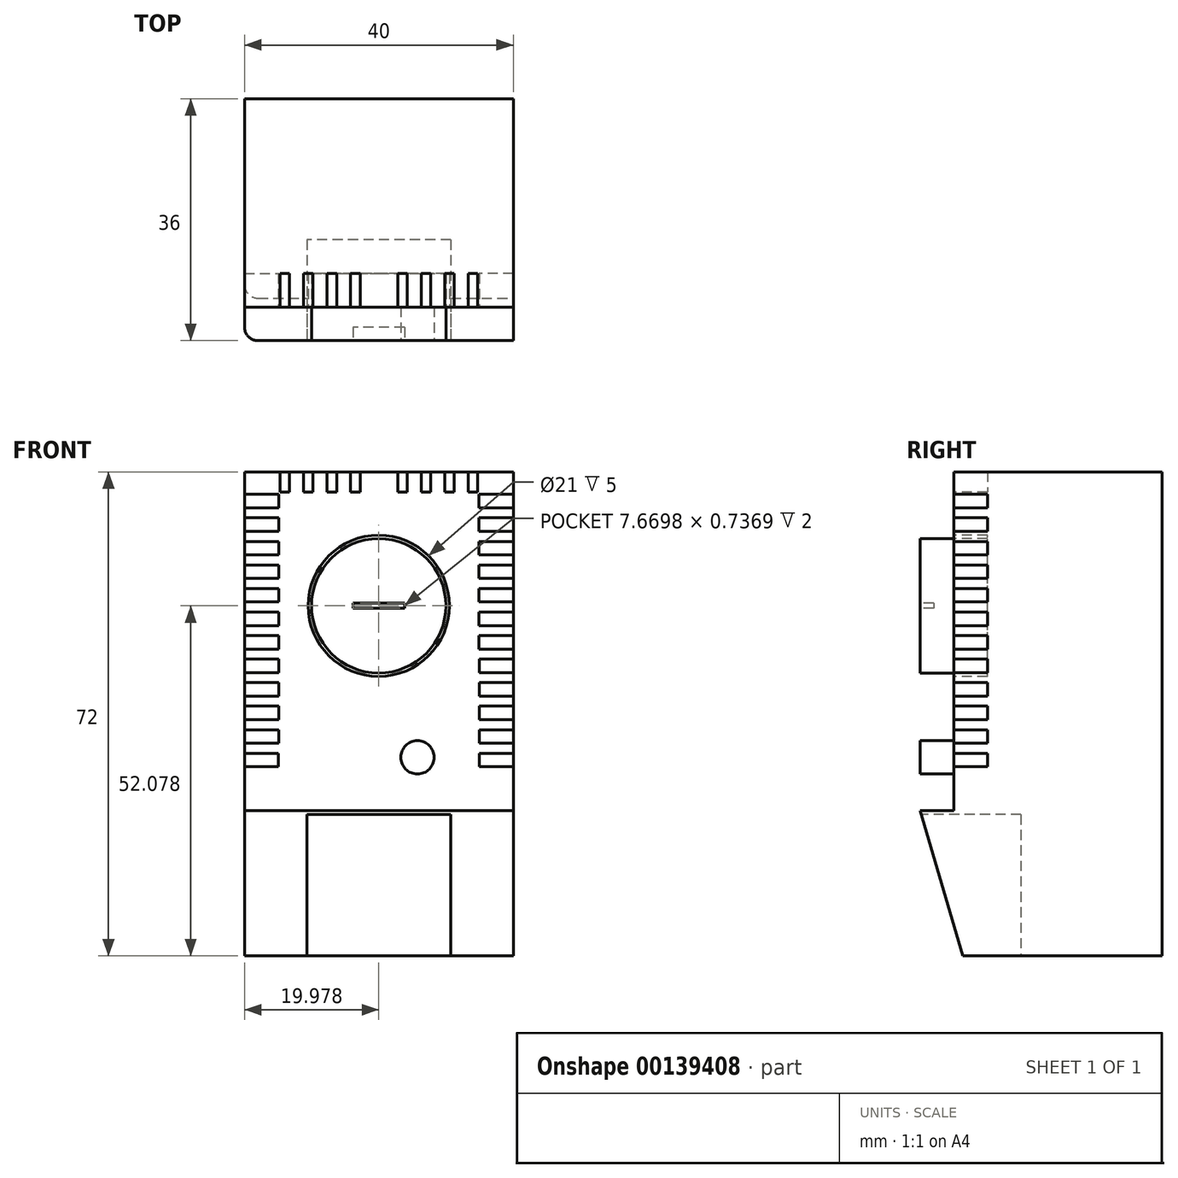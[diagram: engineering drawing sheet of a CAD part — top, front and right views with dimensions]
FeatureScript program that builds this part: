
annotation { "Feature Type Name" : "Feature", "Feature Type Description" : "" }
export const myFeature = defineFeature(function(context is Context, id is Id, definition is map)
    precondition{}
    {
        {
            var Q0;
            Q0=qCreatedBy(makeId("Front.planeOp"),FACE);
            var sketch = newSketch(context, id + "F0", { "sketchPlane" : qUnion([Q0])});
            skLineSegment(sketch, "E0.bottom", {"start": v(-33, 26.48) * mm, "end": v(7, 26.48) * mm});
            skLineSegment(sketch, "E0.top", {"start": v(-33, -45.52) * mm, "end": v(7, -45.52) * mm});
            skLineSegment(sketch, "E0.left", {"start": v(-33, 26.48) * mm, "end": v(-33, -45.52) * mm});
            skLineSegment(sketch, "E0.right", {"start": v(7, 26.48) * mm, "end": v(7, -45.52) * mm});
            skSolve(sketch);
        }
        {
            var Q0;
            Q0=makeQuery(id+"F0.imprint","IMPRINT",FACE,{"disambiguationData":[TD([[makeQuery(id+"F0.imprint","IMPRINT",EDGE,{"derivedFrom":sQuery(id+"F0.wireOp",EDGE,"E0.bottom")}),-1.0]])]});
            extrude(context, id + "F1", {"entities" : qUnion([Q0]), "depth" : 36 * mm});
        }
        {
            var Q0;
            Q0=makeQuery(id+"F1.opExtrude","CAP_FACE",FACE,{"disambiguationData":[OSD([sQuery(id+"F0.wireOp",EDGE,"E0.bottom"),sQuery(id+"F0.wireOp",EDGE,"E0.top"),sQuery(id+"F0.wireOp",EDGE,"E0.left"),sQuery(id+"F0.wireOp",EDGE,"E0.right")])],"isStart":false});
            var sketch = newSketch(context, id + "F2", { "sketchPlane" : qUnion([Q0])});
            skCircle(sketch, "E1", {"center": v(-13.03, 6.56) * mm, "radius": 10 * mm});
            skCircle(sketch, "E2.0", {"center": v(-13.03, 6.56) * mm, "radius": 10.5 * mm});
            skLineSegment(sketch, "E3.bottom", {"start": v(-9.1, 7.18) * mm, "end": v(-16.96, 7.18) * mm});
            skLineSegment(sketch, "E3.top", {"start": v(-9.1, 5.94) * mm, "end": v(-16.96, 5.94) * mm});
            skLineSegment(sketch, "E3.left", {"start": v(-9.1, 7.18) * mm, "end": v(-9.1, 5.94) * mm});
            skLineSegment(sketch, "E3.right", {"start": v(-16.96, 7.18) * mm, "end": v(-16.96, 5.94) * mm});
            skLineSegment(sketch, "E4.bottom", {"start": v(-33, 23.12) * mm, "end": v(-27.9, 23.12) * mm});
            skLineSegment(sketch, "E4.top", {"start": v(-33, 21.12) * mm, "end": v(-27.9, 21.12) * mm});
            skLineSegment(sketch, "E4.left", {"start": v(-33, 23.12) * mm, "end": v(-33, 21.12) * mm});
            skLineSegment(sketch, "E4.right", {"start": v(-27.9, 23.12) * mm, "end": v(-27.9, 21.12) * mm});
            skLineSegment(sketch, "E5.top", {"start": v(-12.3, 23.45) * mm, "end": v(-13.72, 23.45) * mm});
            skLineSegment(sketch, "E5.left", {"start": v(-12.3, 26.48) * mm, "end": v(-12.3, 23.45) * mm});
            skLineSegment(sketch, "E5.right", {"start": v(-13.72, 26.48) * mm, "end": v(-13.72, 23.45) * mm});
            skPoint(sketch, "E5.middle", {"position": v(-13, 26.48) * mm});
            skLineSegment(sketch, "E6", {"start": v(-13.72, 26.48) * mm, "end": v(-12.3, 26.48) * mm});
            skLineSegment(sketch, "E7.1.0.0", {"start": v(-33, 19.62) * mm, "end": v(-33, 17.62) * mm});
            skLineSegment(sketch, "E7.1.0.1", {"start": v(-33, 19.62) * mm, "end": v(-27.9, 19.62) * mm});
            skLineSegment(sketch, "E7.1.0.2", {"start": v(-27.9, 19.62) * mm, "end": v(-27.9, 17.62) * mm});
            skLineSegment(sketch, "E7.1.0.3", {"start": v(-33, 17.62) * mm, "end": v(-27.9, 17.62) * mm});
            skLineSegment(sketch, "E7.2.0.0", {"start": v(-33.01, 16.12) * mm, "end": v(-33.01, 14.12) * mm});
            skLineSegment(sketch, "E7.2.0.1", {"start": v(-33.01, 16.12) * mm, "end": v(-27.9, 16.12) * mm});
            skLineSegment(sketch, "E7.2.0.2", {"start": v(-27.9, 16.12) * mm, "end": v(-27.9, 14.12) * mm});
            skLineSegment(sketch, "E7.2.0.3", {"start": v(-33.01, 14.12) * mm, "end": v(-27.9, 14.12) * mm});
            skLineSegment(sketch, "E7.3.0.0", {"start": v(-33.02, 12.62) * mm, "end": v(-33.02, 10.62) * mm});
            skLineSegment(sketch, "E7.3.0.1", {"start": v(-33.02, 12.62) * mm, "end": v(-27.9, 12.62) * mm});
            skLineSegment(sketch, "E7.3.0.2", {"start": v(-27.9, 12.62) * mm, "end": v(-27.9, 10.62) * mm});
            skLineSegment(sketch, "E7.3.0.3", {"start": v(-33.02, 10.62) * mm, "end": v(-27.9, 10.62) * mm});
            skLineSegment(sketch, "E7.4.0.0", {"start": v(-33.02, 9.12) * mm, "end": v(-33.02, 7.12) * mm});
            skLineSegment(sketch, "E7.4.0.1", {"start": v(-33.02, 9.12) * mm, "end": v(-27.91, 9.12) * mm});
            skLineSegment(sketch, "E7.4.0.2", {"start": v(-27.91, 9.12) * mm, "end": v(-27.91, 7.12) * mm});
            skLineSegment(sketch, "E7.4.0.3", {"start": v(-33.02, 7.12) * mm, "end": v(-27.91, 7.12) * mm});
            skLineSegment(sketch, "E7.5.0.0", {"start": v(-33.02, 5.62) * mm, "end": v(-33.02, 3.62) * mm});
            skLineSegment(sketch, "E7.5.0.1", {"start": v(-33.02, 5.62) * mm, "end": v(-27.91, 5.62) * mm});
            skLineSegment(sketch, "E7.5.0.2", {"start": v(-27.91, 5.62) * mm, "end": v(-27.91, 3.62) * mm});
            skLineSegment(sketch, "E7.5.0.3", {"start": v(-33.02, 3.62) * mm, "end": v(-27.91, 3.62) * mm});
            skLineSegment(sketch, "E7.6.0.0", {"start": v(-33.03, 2.12) * mm, "end": v(-33.03, 0.12) * mm});
            skLineSegment(sketch, "E7.6.0.1", {"start": v(-33.03, 2.12) * mm, "end": v(-27.92, 2.12) * mm});
            skLineSegment(sketch, "E7.6.0.2", {"start": v(-27.92, 2.12) * mm, "end": v(-27.92, 0.12) * mm});
            skLineSegment(sketch, "E7.6.0.3", {"start": v(-33.03, 0.12) * mm, "end": v(-27.92, 0.12) * mm});
            skLineSegment(sketch, "E7.7.0.0", {"start": v(-33.03, -1.38) * mm, "end": v(-33.03, -3.38) * mm});
            skLineSegment(sketch, "E7.7.0.1", {"start": v(-33.03, -1.38) * mm, "end": v(-27.92, -1.38) * mm});
            skLineSegment(sketch, "E7.7.0.2", {"start": v(-27.92, -1.38) * mm, "end": v(-27.92, -3.38) * mm});
            skLineSegment(sketch, "E7.7.0.3", {"start": v(-33.03, -3.38) * mm, "end": v(-27.92, -3.38) * mm});
            skLineSegment(sketch, "E7.8.0.0", {"start": v(-33.04, -4.88) * mm, "end": v(-33.04, -6.88) * mm});
            skLineSegment(sketch, "E7.8.0.1", {"start": v(-33.04, -4.88) * mm, "end": v(-27.93, -4.88) * mm});
            skLineSegment(sketch, "E7.8.0.2", {"start": v(-27.93, -4.88) * mm, "end": v(-27.93, -6.88) * mm});
            skLineSegment(sketch, "E7.8.0.3", {"start": v(-33.04, -6.88) * mm, "end": v(-27.93, -6.88) * mm});
            skLineSegment(sketch, "E7.9.0.0", {"start": v(-33.04, -8.38) * mm, "end": v(-33.04, -10.38) * mm});
            skLineSegment(sketch, "E7.9.0.1", {"start": v(-33.04, -8.38) * mm, "end": v(-27.93, -8.38) * mm});
            skLineSegment(sketch, "E7.9.0.2", {"start": v(-27.93, -8.38) * mm, "end": v(-27.93, -10.38) * mm});
            skLineSegment(sketch, "E7.9.0.3", {"start": v(-33.04, -10.38) * mm, "end": v(-27.93, -10.38) * mm});
            skLineSegment(sketch, "E7.10.0.0", {"start": v(-33.04, -11.88) * mm, "end": v(-33.04, -13.88) * mm});
            skLineSegment(sketch, "E7.10.0.1", {"start": v(-33.04, -11.88) * mm, "end": v(-27.93, -11.88) * mm});
            skLineSegment(sketch, "E7.10.0.2", {"start": v(-27.93, -11.88) * mm, "end": v(-27.93, -13.88) * mm});
            skLineSegment(sketch, "E7.10.0.3", {"start": v(-33.04, -13.88) * mm, "end": v(-27.93, -13.88) * mm});
            skLineSegment(sketch, "E7.11.0.0", {"start": v(-33.05, -15.38) * mm, "end": v(-33.05, -17.38) * mm});
            skLineSegment(sketch, "E7.11.0.1", {"start": v(-33.05, -15.38) * mm, "end": v(-27.94, -15.38) * mm});
            skLineSegment(sketch, "E7.11.0.2", {"start": v(-27.94, -15.38) * mm, "end": v(-27.94, -17.38) * mm});
            skLineSegment(sketch, "E7.11.0.3", {"start": v(-33.05, -17.38) * mm, "end": v(-27.94, -17.38) * mm});
            skLineSegment(sketch, "E7.direction1", {"start": v(-33, 21.12) * mm, "end": v(-33, 17.62) * mm, "construction": true});
            skLineSegment(sketch, "E8.1.0.0", {"start": v(-8.8, 23.45) * mm, "end": v(-10.22, 23.45) * mm});
            skLineSegment(sketch, "E8.1.0.1", {"start": v(-8.8, 26.48) * mm, "end": v(-8.8, 23.45) * mm});
            skPoint(sketch, "E8.1.0.2", {"position": v(-9.5, 26.48) * mm});
            skLineSegment(sketch, "E8.1.0.3", {"start": v(-10.22, 26.48) * mm, "end": v(-10.22, 23.45) * mm});
            skLineSegment(sketch, "E8.1.0.4", {"start": v(-10.22, 26.48) * mm, "end": v(-8.8, 26.48) * mm});
            skLineSegment(sketch, "E8.2.0.0", {"start": v(-5.3, 23.45) * mm, "end": v(-6.72, 23.45) * mm});
            skLineSegment(sketch, "E8.2.0.1", {"start": v(-5.3, 26.48) * mm, "end": v(-5.3, 23.45) * mm});
            skPoint(sketch, "E8.2.0.2", {"position": v(-6, 26.48) * mm});
            skLineSegment(sketch, "E8.2.0.3", {"start": v(-6.72, 26.48) * mm, "end": v(-6.72, 23.45) * mm});
            skLineSegment(sketch, "E8.2.0.4", {"start": v(-6.72, 26.48) * mm, "end": v(-5.3, 26.48) * mm});
            skLineSegment(sketch, "E8.3.0.0", {"start": v(-1.8, 23.45) * mm, "end": v(-3.22, 23.45) * mm});
            skLineSegment(sketch, "E8.3.0.1", {"start": v(-1.8, 26.48) * mm, "end": v(-1.8, 23.45) * mm});
            skPoint(sketch, "E8.3.0.2", {"position": v(-2.5, 26.48) * mm});
            skLineSegment(sketch, "E8.3.0.3", {"start": v(-3.22, 26.48) * mm, "end": v(-3.22, 23.45) * mm});
            skLineSegment(sketch, "E8.3.0.4", {"start": v(-3.22, 26.48) * mm, "end": v(-1.8, 26.48) * mm});
            skLineSegment(sketch, "E8.4.0.0", {"start": v(1.7, 23.45) * mm, "end": v(0.28, 23.45) * mm});
            skLineSegment(sketch, "E8.4.0.1", {"start": v(1.7, 26.48) * mm, "end": v(1.7, 23.45) * mm});
            skPoint(sketch, "E8.4.0.2", {"position": v(1, 26.48) * mm});
            skLineSegment(sketch, "E8.4.0.3", {"start": v(0.28, 26.48) * mm, "end": v(0.28, 23.45) * mm});
            skLineSegment(sketch, "E8.4.0.4", {"start": v(0.28, 26.48) * mm, "end": v(1.7, 26.48) * mm});
            skLineSegment(sketch, "E8.direction1", {"start": v(-13.72, 23.45) * mm, "end": v(-10.22, 23.45) * mm, "construction": true});
            skLineSegment(sketch, "E9", {"start": v(-13, 26.48) * mm, "end": v(-13, 37.21) * mm});
            skLineSegment(sketch, "E10.MirrorCS", {"start": v(-15.8, 26.48) * mm, "end": v(-17.22, 26.48) * mm});
            skLineSegment(sketch, "E11.MirrorCS", {"start": v(-26.3, 26.48) * mm, "end": v(-27.72, 26.48) * mm});
            skLineSegment(sketch, "E12.MirrorCS", {"start": v(-22.8, 26.48) * mm, "end": v(-24.22, 26.48) * mm});
            skLineSegment(sketch, "E13.MirrorCS", {"start": v(-20.72, 23.45) * mm, "end": v(-19.3, 23.45) * mm});
            skLineSegment(sketch, "E14.MirrorCS", {"start": v(-19.3, 26.48) * mm, "end": v(-20.72, 26.48) * mm});
            skLineSegment(sketch, "E15.MirrorCS", {"start": v(-24.22, 23.45) * mm, "end": v(-22.8, 23.45) * mm});
            skLineSegment(sketch, "E16.MirrorCS", {"start": v(-27.72, 23.45) * mm, "end": v(-26.3, 23.45) * mm});
            skLineSegment(sketch, "E17.MirrorCS", {"start": v(-17.22, 23.45) * mm, "end": v(-15.8, 23.45) * mm});
            skLineSegment(sketch, "E18.MirrorCS", {"start": v(-15.8, 26.48) * mm, "end": v(-15.8, 23.45) * mm});
            skLineSegment(sketch, "E19.MirrorCS", {"start": v(-24.22, 26.48) * mm, "end": v(-24.22, 23.45) * mm});
            skLineSegment(sketch, "E20.MirrorCS", {"start": v(-17.22, 26.48) * mm, "end": v(-17.22, 23.45) * mm});
            skPoint(sketch, "E21.MirrorP", {"position": v(-27, 26.48) * mm});
            skLineSegment(sketch, "E22.MirrorCS", {"start": v(-22.8, 26.48) * mm, "end": v(-22.8, 23.45) * mm});
            skLineSegment(sketch, "E23.MirrorCS", {"start": v(-26.3, 26.48) * mm, "end": v(-26.3, 23.45) * mm});
            skPoint(sketch, "E24.MirrorP", {"position": v(-20, 26.48) * mm});
            skLineSegment(sketch, "E25.MirrorCS", {"start": v(-27.72, 26.48) * mm, "end": v(-27.72, 23.45) * mm});
            skLineSegment(sketch, "E26.MirrorCS", {"start": v(-19.3, 26.48) * mm, "end": v(-19.3, 23.45) * mm});
            skLineSegment(sketch, "E27.MirrorCS", {"start": v(-20.72, 26.48) * mm, "end": v(-20.72, 23.45) * mm});
            skPoint(sketch, "E28.MirrorP", {"position": v(-23.5, 26.48) * mm});
            skPoint(sketch, "E29.MirrorP", {"position": v(-16.5, 26.48) * mm});
            skLineSegment(sketch, "E30.MirrorCS", {"start": v(7, 19.62) * mm, "end": v(7, 17.62) * mm});
            skLineSegment(sketch, "E31.MirrorCS", {"start": v(7.02, 2.12) * mm, "end": v(7.02, 0.12) * mm});
            skLineSegment(sketch, "E32.MirrorCS", {"start": v(7, 23.12) * mm, "end": v(7, 21.12) * mm});
            skLineSegment(sketch, "E33.MirrorCS", {"start": v(1.88, 23.12) * mm, "end": v(1.88, 21.12) * mm});
            skLineSegment(sketch, "E34.MirrorCS", {"start": v(1.91, -1.38) * mm, "end": v(1.91, -3.38) * mm});
            skLineSegment(sketch, "E35.MirrorCS", {"start": v(1.92, -8.38) * mm, "end": v(1.92, -10.38) * mm});
            skLineSegment(sketch, "E36.MirrorCS", {"start": v(7, 23.12) * mm, "end": v(1.88, 23.12) * mm});
            skLineSegment(sketch, "E37.MirrorCS", {"start": v(1.9, 5.62) * mm, "end": v(1.9, 3.62) * mm});
            skLineSegment(sketch, "E38.MirrorCS", {"start": v(1.9, 2.12) * mm, "end": v(1.9, 0.12) * mm});
            skLineSegment(sketch, "E39.MirrorCS", {"start": v(1.93, -15.38) * mm, "end": v(1.93, -17.38) * mm});
            skLineSegment(sketch, "E40.MirrorCS", {"start": v(7.03, -8.38) * mm, "end": v(7.03, -10.38) * mm});
            skLineSegment(sketch, "E41.MirrorCS", {"start": v(7.02, -1.38) * mm, "end": v(7.02, -3.38) * mm});
            skLineSegment(sketch, "E42.MirrorCS", {"start": v(1.89, 19.62) * mm, "end": v(1.89, 17.62) * mm});
            skLineSegment(sketch, "E43.MirrorCS", {"start": v(1.9, 9.12) * mm, "end": v(1.9, 7.12) * mm});
            skLineSegment(sketch, "E44.MirrorCS", {"start": v(7, 9.12) * mm, "end": v(7, 7.12) * mm});
            skLineSegment(sketch, "E45.MirrorCS", {"start": v(7.02, -4.88) * mm, "end": v(7.02, -6.88) * mm});
            skLineSegment(sketch, "E46.MirrorCS", {"start": v(7, 21.12) * mm, "end": v(7, 17.62) * mm, "construction": true});
            skLineSegment(sketch, "E47.MirrorCS", {"start": v(1.91, -4.88) * mm, "end": v(1.91, -6.88) * mm});
            skLineSegment(sketch, "E48.MirrorCS", {"start": v(1.9, 16.12) * mm, "end": v(1.9, 14.12) * mm});
            skLineSegment(sketch, "E49.MirrorCS", {"start": v(7, 16.12) * mm, "end": v(7, 14.12) * mm});
            skLineSegment(sketch, "E50.MirrorCS", {"start": v(1.9, 12.62) * mm, "end": v(1.9, 10.62) * mm});
            skLineSegment(sketch, "E51.MirrorCS", {"start": v(7.03, -11.88) * mm, "end": v(7.03, -13.88) * mm});
            skLineSegment(sketch, "E52.MirrorCS", {"start": v(7, 12.62) * mm, "end": v(7, 10.62) * mm});
            skLineSegment(sketch, "E53.MirrorCS", {"start": v(1.92, -11.88) * mm, "end": v(1.92, -13.88) * mm});
            skLineSegment(sketch, "E54.MirrorCS", {"start": v(7.01, 5.62) * mm, "end": v(7.01, 3.62) * mm});
            skLineSegment(sketch, "E55.MirrorCS", {"start": v(7.04, -15.38) * mm, "end": v(7.04, -17.38) * mm});
            skLineSegment(sketch, "E56.MirrorCS", {"start": v(7.03, -11.88) * mm, "end": v(1.92, -11.88) * mm});
            skLineSegment(sketch, "E57.MirrorCS", {"start": v(7, 21.12) * mm, "end": v(1.88, 21.12) * mm});
            skLineSegment(sketch, "E58.MirrorCS", {"start": v(7.03, -8.38) * mm, "end": v(1.92, -8.38) * mm});
            skLineSegment(sketch, "E59.MirrorCS", {"start": v(7.03, -10.38) * mm, "end": v(1.92, -10.38) * mm});
            skLineSegment(sketch, "E60.MirrorCS", {"start": v(7.03, -13.88) * mm, "end": v(1.92, -13.88) * mm});
            skLineSegment(sketch, "E61.MirrorCS", {"start": v(7, 16.12) * mm, "end": v(1.9, 16.12) * mm});
            skLineSegment(sketch, "E62.MirrorCS", {"start": v(7, 17.62) * mm, "end": v(1.89, 17.62) * mm});
            skLineSegment(sketch, "E63.MirrorCS", {"start": v(7.02, 2.12) * mm, "end": v(1.9, 2.12) * mm});
            skLineSegment(sketch, "E64.MirrorCS", {"start": v(7, 10.62) * mm, "end": v(1.9, 10.62) * mm});
            skLineSegment(sketch, "E65.MirrorCS", {"start": v(7.02, -3.38) * mm, "end": v(1.91, -3.38) * mm});
            skLineSegment(sketch, "E66.MirrorCS", {"start": v(7.01, 3.62) * mm, "end": v(1.9, 3.62) * mm});
            skLineSegment(sketch, "E67.MirrorCS", {"start": v(7.04, -17.38) * mm, "end": v(1.93, -17.38) * mm});
            skLineSegment(sketch, "E68.MirrorCS", {"start": v(7, 19.62) * mm, "end": v(1.89, 19.62) * mm});
            skLineSegment(sketch, "E69.MirrorCS", {"start": v(7, 9.12) * mm, "end": v(1.9, 9.12) * mm});
            skLineSegment(sketch, "E70.MirrorCS", {"start": v(7, 7.12) * mm, "end": v(1.9, 7.12) * mm});
            skLineSegment(sketch, "E71.MirrorCS", {"start": v(7.02, 0.12) * mm, "end": v(1.9, 0.12) * mm});
            skLineSegment(sketch, "E72.MirrorCS", {"start": v(7, 12.62) * mm, "end": v(1.9, 12.62) * mm});
            skLineSegment(sketch, "E73.MirrorCS", {"start": v(7.02, -6.88) * mm, "end": v(1.91, -6.88) * mm});
            skLineSegment(sketch, "E74.MirrorCS", {"start": v(7, 14.12) * mm, "end": v(1.9, 14.12) * mm});
            skLineSegment(sketch, "E75.MirrorCS", {"start": v(7.02, -4.88) * mm, "end": v(1.91, -4.88) * mm});
            skLineSegment(sketch, "E76.MirrorCS", {"start": v(7.01, 5.62) * mm, "end": v(1.9, 5.62) * mm});
            skLineSegment(sketch, "E77.MirrorCS", {"start": v(7.04, -15.38) * mm, "end": v(1.93, -15.38) * mm});
            skLineSegment(sketch, "E78.MirrorCS", {"start": v(7.02, -1.38) * mm, "end": v(1.91, -1.38) * mm});
            skSolve(sketch);
        }
        {
            var Q0;
            Q0=makeQuery(id+"F2.imprint","IMPRINT",FACE,{"disambiguationData":[TD([[makeQuery(id+"F2.imprint","IMPRINT",EDGE,{"derivedFrom":sQuery(id+"F2.wireOp",EDGE,"E4.bottom")}),-1.0]])]});
            var Q1;
            {var subQ0=sQuery(id+"F2.wireOp",EDGE,"E7.1.0.2");Q1=makeQuery(id+"F2.imprint","IMPRINT",FACE,{"disambiguationData":[TD([[makeQuery(id+"F2.imprint","IMPRINT",EDGE,{"derivedFrom":subQ0}),-1.0]])]});}
            var Q2;
            {var subQ0=sQuery(id+"F2.wireOp",EDGE,"E7.2.0.2");Q2=makeQuery(id+"F2.imprint","IMPRINT",FACE,{"disambiguationData":[TD([[makeQuery(id+"F2.imprint","IMPRINT",EDGE,{"derivedFrom":subQ0}),-1.0]])]});}
            var Q3;
            {var subQ0=sQuery(id+"F2.wireOp",EDGE,"E7.3.0.2");Q3=makeQuery(id+"F2.imprint","IMPRINT",FACE,{"disambiguationData":[TD([[makeQuery(id+"F2.imprint","IMPRINT",EDGE,{"derivedFrom":subQ0}),-1.0]])]});}
            var Q4;
            {var subQ0=sQuery(id+"F2.wireOp",EDGE,"E7.4.0.2");Q4=makeQuery(id+"F2.imprint","IMPRINT",FACE,{"disambiguationData":[TD([[makeQuery(id+"F2.imprint","IMPRINT",EDGE,{"derivedFrom":subQ0}),-1.0]])]});}
            var Q5;
            {var subQ0=sQuery(id+"F2.wireOp",EDGE,"E7.5.0.2");Q5=makeQuery(id+"F2.imprint","IMPRINT",FACE,{"disambiguationData":[TD([[makeQuery(id+"F2.imprint","IMPRINT",EDGE,{"derivedFrom":subQ0}),-1.0]])]});}
            var Q6;
            {var subQ0=sQuery(id+"F2.wireOp",EDGE,"E7.6.0.2");Q6=makeQuery(id+"F2.imprint","IMPRINT",FACE,{"disambiguationData":[TD([[makeQuery(id+"F2.imprint","IMPRINT",EDGE,{"derivedFrom":subQ0}),-1.0]])]});}
            var Q7;
            {var subQ0=sQuery(id+"F2.wireOp",EDGE,"E7.7.0.2");Q7=makeQuery(id+"F2.imprint","IMPRINT",FACE,{"disambiguationData":[TD([[makeQuery(id+"F2.imprint","IMPRINT",EDGE,{"derivedFrom":subQ0}),-1.0]])]});}
            var Q8;
            {var subQ0=sQuery(id+"F2.wireOp",EDGE,"E7.8.0.2");Q8=makeQuery(id+"F2.imprint","IMPRINT",FACE,{"disambiguationData":[TD([[makeQuery(id+"F2.imprint","IMPRINT",EDGE,{"derivedFrom":subQ0}),-1.0]])]});}
            var Q9;
            {var subQ0=sQuery(id+"F2.wireOp",EDGE,"E7.9.0.2");Q9=makeQuery(id+"F2.imprint","IMPRINT",FACE,{"disambiguationData":[TD([[makeQuery(id+"F2.imprint","IMPRINT",EDGE,{"derivedFrom":subQ0}),-1.0]])]});}
            var Q10;
            {var subQ0=sQuery(id+"F2.wireOp",EDGE,"E7.10.0.2");Q10=makeQuery(id+"F2.imprint","IMPRINT",FACE,{"disambiguationData":[TD([[makeQuery(id+"F2.imprint","IMPRINT",EDGE,{"derivedFrom":subQ0}),-1.0]])]});}
            var Q11;
            {var subQ0=sQuery(id+"F2.wireOp",EDGE,"E7.11.0.2");Q11=makeQuery(id+"F2.imprint","IMPRINT",FACE,{"disambiguationData":[TD([[makeQuery(id+"F2.imprint","IMPRINT",EDGE,{"derivedFrom":subQ0}),-1.0]])]});}
            var Q12;
            {var subQ0=sQuery(id+"F2.wireOp",EDGE,"E39.MirrorCS");Q12=makeQuery(id+"F2.imprint","IMPRINT",FACE,{"disambiguationData":[TD([[makeQuery(id+"F2.imprint","IMPRINT",EDGE,{"derivedFrom":subQ0}),1.0]])]});}
            var Q13;
            {var subQ0=sQuery(id+"F2.wireOp",EDGE,"E53.MirrorCS");Q13=makeQuery(id+"F2.imprint","IMPRINT",FACE,{"disambiguationData":[TD([[makeQuery(id+"F2.imprint","IMPRINT",EDGE,{"derivedFrom":subQ0}),1.0]])]});}
            var Q14;
            {var subQ0=sQuery(id+"F2.wireOp",EDGE,"E35.MirrorCS");Q14=makeQuery(id+"F2.imprint","IMPRINT",FACE,{"disambiguationData":[TD([[makeQuery(id+"F2.imprint","IMPRINT",EDGE,{"derivedFrom":subQ0}),1.0]])]});}
            var Q15;
            {var subQ0=sQuery(id+"F2.wireOp",EDGE,"E47.MirrorCS");Q15=makeQuery(id+"F2.imprint","IMPRINT",FACE,{"disambiguationData":[TD([[makeQuery(id+"F2.imprint","IMPRINT",EDGE,{"derivedFrom":subQ0}),1.0]])]});}
            var Q16;
            {var subQ0=sQuery(id+"F2.wireOp",EDGE,"E38.MirrorCS");Q16=makeQuery(id+"F2.imprint","IMPRINT",FACE,{"disambiguationData":[TD([[makeQuery(id+"F2.imprint","IMPRINT",EDGE,{"derivedFrom":subQ0}),1.0]])]});}
            var Q17;
            {var subQ0=sQuery(id+"F2.wireOp",EDGE,"E37.MirrorCS");Q17=makeQuery(id+"F2.imprint","IMPRINT",FACE,{"disambiguationData":[TD([[makeQuery(id+"F2.imprint","IMPRINT",EDGE,{"derivedFrom":subQ0}),1.0]])]});}
            var Q18;
            {var subQ0=sQuery(id+"F2.wireOp",EDGE,"E43.MirrorCS");Q18=makeQuery(id+"F2.imprint","IMPRINT",FACE,{"disambiguationData":[TD([[makeQuery(id+"F2.imprint","IMPRINT",EDGE,{"derivedFrom":subQ0}),1.0]])]});}
            var Q19;
            {var subQ0=sQuery(id+"F2.wireOp",EDGE,"E50.MirrorCS");Q19=makeQuery(id+"F2.imprint","IMPRINT",FACE,{"disambiguationData":[TD([[makeQuery(id+"F2.imprint","IMPRINT",EDGE,{"derivedFrom":subQ0}),1.0]])]});}
            var Q20;
            {var subQ0=sQuery(id+"F2.wireOp",EDGE,"E48.MirrorCS");Q20=makeQuery(id+"F2.imprint","IMPRINT",FACE,{"disambiguationData":[TD([[makeQuery(id+"F2.imprint","IMPRINT",EDGE,{"derivedFrom":subQ0}),1.0]])]});}
            var Q21;
            {var subQ0=sQuery(id+"F2.wireOp",EDGE,"E42.MirrorCS");Q21=makeQuery(id+"F2.imprint","IMPRINT",FACE,{"disambiguationData":[TD([[makeQuery(id+"F2.imprint","IMPRINT",EDGE,{"derivedFrom":subQ0}),1.0]])]});}
            var Q22;
            Q22=makeQuery(id+"F2.imprint","IMPRINT",FACE,{"disambiguationData":[TD([[makeQuery(id+"F2.imprint","IMPRINT",EDGE,{"derivedFrom":sQuery(id+"F2.wireOp",EDGE,"E32.MirrorCS")}),-1.0]])]});
            var Q23;
            Q23=makeQuery(id+"F2.imprint","IMPRINT",FACE,{"disambiguationData":[TD([[makeQuery(id+"F2.imprint","IMPRINT",EDGE,{"derivedFrom":sQuery(id+"F2.wireOp",EDGE,"E8.4.0.0")}),-1.0]])]});
            var Q24;
            Q24=makeQuery(id+"F2.imprint","IMPRINT",FACE,{"disambiguationData":[TD([[makeQuery(id+"F2.imprint","IMPRINT",EDGE,{"derivedFrom":sQuery(id+"F2.wireOp",EDGE,"E8.3.0.0")}),-1.0]])]});
            var Q25;
            Q25=makeQuery(id+"F2.imprint","IMPRINT",FACE,{"disambiguationData":[TD([[makeQuery(id+"F2.imprint","IMPRINT",EDGE,{"derivedFrom":sQuery(id+"F2.wireOp",EDGE,"E8.2.0.0")}),-1.0]])]});
            var Q26;
            Q26=makeQuery(id+"F2.imprint","IMPRINT",FACE,{"disambiguationData":[TD([[makeQuery(id+"F2.imprint","IMPRINT",EDGE,{"derivedFrom":sQuery(id+"F2.wireOp",EDGE,"E8.1.0.0")}),-1.0]])]});
            var Q27;
            Q27=makeQuery(id+"F2.imprint","IMPRINT",FACE,{"disambiguationData":[TD([[makeQuery(id+"F2.imprint","IMPRINT",EDGE,{"derivedFrom":sQuery(id+"F2.wireOp",EDGE,"E10.MirrorCS")}),-1.0]])]});
            var Q28;
            Q28=makeQuery(id+"F2.imprint","IMPRINT",FACE,{"disambiguationData":[TD([[makeQuery(id+"F2.imprint","IMPRINT",EDGE,{"derivedFrom":sQuery(id+"F2.wireOp",EDGE,"E13.MirrorCS")}),1.0]])]});
            var Q29;
            Q29=makeQuery(id+"F2.imprint","IMPRINT",FACE,{"disambiguationData":[TD([[makeQuery(id+"F2.imprint","IMPRINT",EDGE,{"derivedFrom":sQuery(id+"F2.wireOp",EDGE,"E12.MirrorCS")}),-1.0]])]});
            var Q30;
            Q30=makeQuery(id+"F2.imprint","IMPRINT",FACE,{"disambiguationData":[TD([[makeQuery(id+"F2.imprint","IMPRINT",EDGE,{"derivedFrom":sQuery(id+"F2.wireOp",EDGE,"E11.MirrorCS")}),-1.0]])]});
            var Q31;
            {var subQ0=sQuery(id+"F2.wireOp",EDGE,"E34.MirrorCS");Q31=makeQuery(id+"F2.imprint","IMPRINT",FACE,{"disambiguationData":[TD([[makeQuery(id+"F2.imprint","IMPRINT",EDGE,{"derivedFrom":subQ0}),1.0]])]});}
            var Q32;
            Q32=makeQuery(id+"F2.imprint","IMPRINT",FACE,{"disambiguationData":[TD([[makeQuery(id+"F2.imprint","IMPRINT",EDGE,{"derivedFrom":sQuery(id+"F2.wireOp",EDGE,"E1")}),-1.0]])]});
            extrude(context, id + "F3", {"entities" : qUnion([Q0, Q1, Q2, Q3, Q4, Q5, Q6, Q7, Q8, Q9, Q10, Q11, Q12, Q13, Q14, Q15, Q16, Q17, Q18, Q19, Q20, Q21, Q22, Q23, Q24, Q25, Q26, Q27, Q28, Q29, Q30, Q31, Q32]), "operationType" : NewBodyOperationType.REMOVE, "oppositeDirection" : true, "depth" : 10 * mm});
        }
        {
            var Q0;
            Q0=makeQuery(id+"F3.boolean.opBoolean","SPLIT",FACE,{"disambiguationData":[TD([makeQuery(id+"F3.opExtrude","SWEPT_FACE",FACE,{"disambiguationData":[OSD([sQuery(id+"F2.wireOp",EDGE,"E1")])]})])],"derivedFrom":makeQuery(id+"F1.opExtrude","CAP_FACE",FACE,{"disambiguationData":[OSD([sQuery(id+"F0.wireOp",EDGE,"E0.bottom"),sQuery(id+"F0.wireOp",EDGE,"E0.top"),sQuery(id+"F0.wireOp",EDGE,"E0.left"),sQuery(id+"F0.wireOp",EDGE,"E0.right")])],"isStart":false})});
            var sketch = newSketch(context, id + "F4", { "sketchPlane" : qUnion([Q0])});
            skPoint(sketch, "E79", {"position": v(-13.03, 6.56) * mm});
            skLineSegment(sketch, "E80.bottom", {"start": v(-9.2, 6.93) * mm, "end": v(-16.87, 6.93) * mm});
            skLineSegment(sketch, "E80.top", {"start": v(-9.2, 6.19) * mm, "end": v(-16.87, 6.19) * mm});
            skLineSegment(sketch, "E80.left", {"start": v(-9.2, 6.93) * mm, "end": v(-9.2, 6.19) * mm});
            skLineSegment(sketch, "E80.right", {"start": v(-16.87, 6.93) * mm, "end": v(-16.87, 6.19) * mm});
            skSolve(sketch);
        }
        {
            var Q0;
            Q0=makeQuery(id+"F4.imprint","IMPRINT",FACE,{"disambiguationData":[TD([[makeQuery(id+"F4.imprint","IMPRINT",EDGE,{"derivedFrom":sQuery(id+"F4.wireOp",EDGE,"E80.bottom")}),1.0]])]});
            extrude(context, id + "F5", {"entities" : qUnion([Q0]), "operationType" : NewBodyOperationType.REMOVE, "oppositeDirection" : true, "depth" : 2 * mm});
        }
        {
            var Q0;
            {var subQ0=sQuery(id+"F0.wireOp",EDGE,"E0.right");var subQ1=sQuery(id+"F0.wireOp",EDGE,"E0.top");var subQ2=sQuery(id+"F0.wireOp",EDGE,"E0.left");var subQ3=sQuery(id+"F0.wireOp",EDGE,"E0.bottom");Q0=makeQuery(id+"F3.boolean.opBoolean","SPLIT",FACE,{"disambiguationData":[TD([makeQuery(id+"F1.opExtrude","SWEPT_FACE",FACE,{"disambiguationData":[OSD([subQ3])]})])],"derivedFrom":makeQuery(id+"F1.opExtrude","CAP_FACE",FACE,{"disambiguationData":[OSD([subQ3,subQ1,subQ2,subQ0])],"isStart":false})});}
            var sketch = newSketch(context, id + "F6", { "sketchPlane" : qUnion([Q0])});
            skLineSegment(sketch, "E81.bottom", {"start": v(-2.3, -24.47) * mm, "end": v(-23.71, -24.47) * mm});
            skLineSegment(sketch, "E81.top", {"start": v(-2.3, -66.57) * mm, "end": v(-23.71, -66.57) * mm});
            skLineSegment(sketch, "E81.left", {"start": v(-2.3, -24.47) * mm, "end": v(-2.3, -66.57) * mm});
            skLineSegment(sketch, "E81.right", {"start": v(-23.71, -24.47) * mm, "end": v(-23.71, -66.57) * mm});
            skPoint(sketch, "E81.middle", {"position": v(-13, -45.52) * mm});
            skSolve(sketch);
        }
        {
            var Q0;
            {var subQ0=sQuery(id+"F6.wireOp",EDGE,"E81.bottom");Q0=makeQuery(id+"F6.imprint","IMPRINT",FACE,{"disambiguationData":[TD([[makeQuery(id+"F6.imprint","IMPRINT",EDGE,{"derivedFrom":subQ0}),1.0]])]});}
            extrude(context, id + "F7", {"entities" : qUnion([Q0]), "operationType" : NewBodyOperationType.REMOVE, "oppositeDirection" : true, "depth" : 15 * mm});
        }
        {
            var Q0;
            Q0=makeQuery(id+"F1.opExtrude","SWEPT_FACE",FACE,{"disambiguationData":[OSD([sQuery(id+"F0.wireOp",EDGE,"E0.right")])]});
            var sketch = newSketch(context, id + "F8", { "sketchPlane" : qUnion([Q0])});
            skLineSegment(sketch, "E82", {"start": v(-36, -23.94) * mm, "end": v(-29.69, -45.52) * mm});
            skSolve(sketch);
        }
        {
            var Q0;
            {var subQ0=sQuery(id+"F8.wireOp",EDGE,"E82");Q0=makeQuery(id+"F8.imprint","IMPRINT",FACE,{"disambiguationData":[TD([[makeQuery(id+"F8.imprint","IMPRINT",EDGE,{"derivedFrom":subQ0}),-1.0]])]});}
            extrude(context, id + "F9", {"entities" : qUnion([Q0]), "operationType" : NewBodyOperationType.REMOVE, "oppositeDirection" : true, "depth" : 50 * mm});
        }
        {
            var Q0;
            {var subQ0=sQuery(id+"F0.wireOp",EDGE,"E0.right");var subQ1=sQuery(id+"F0.wireOp",EDGE,"E0.top");var subQ2=sQuery(id+"F0.wireOp",EDGE,"E0.left");var subQ3=sQuery(id+"F0.wireOp",EDGE,"E0.bottom");Q0=makeQuery(id+"F3.boolean.opBoolean","SPLIT",FACE,{"disambiguationData":[TD([makeQuery(id+"F1.opExtrude","SWEPT_FACE",FACE,{"disambiguationData":[OSD([subQ3])]})])],"derivedFrom":makeQuery(id+"F1.opExtrude","CAP_FACE",FACE,{"disambiguationData":[OSD([subQ3,subQ1,subQ2,subQ0])],"isStart":false})});}
            var sketch = newSketch(context, id + "F10", { "sketchPlane" : qUnion([Q0])});
            skCircle(sketch, "E83", {"center": v(-18.75, -15.98) * mm, "radius": 2.48 * mm});
            skCircle(sketch, "E84.MirrorC", {"center": v(-7.26, -15.98) * mm, "radius": 2.48 * mm});
            skSolve(sketch);
        }
        {
            var Q0;
            Q0=makeQuery(id+"F10.imprint","IMPRINT",FACE,{"disambiguationData":[TD([[makeQuery(id+"F10.imprint","IMPRINT",EDGE,{"derivedFrom":sQuery(id+"F10.wireOp",EDGE,"E83")}),1.0]])]});
            var Q1;
            Q1=makeQuery(id+"F10.imprint","IMPRINT",FACE,{"disambiguationData":[TD([[makeQuery(id+"F10.imprint","IMPRINT",EDGE,{"derivedFrom":sQuery(id+"F10.wireOp",EDGE,"E84.MirrorC")}),-1.0]])]});
            extrude(context, id + "F11", {"entities" : qUnion([Q0, Q1]), "operationType" : NewBodyOperationType.REMOVE, "oppositeDirection" : true, "depth" : 5 * mm});
        }
        {
            var Q0;
            {var subQ0=sQuery(id+"F0.wireOp",EDGE,"E0.bottom");var subQ1=sQuery(id+"F0.wireOp",EDGE,"E0.left");Q0=makeQuery(id+"F3.boolean.opBoolean","SPLIT",EDGE,{"disambiguationData":[TD([makeQuery(id+"F1.opExtrude","SWEPT_FACE",FACE,{"disambiguationData":[OSD([subQ0])]})])],"derivedFrom":makeQuery(id+"F1.opExtrude","CAP_EDGE",EDGE,{"disambiguationData":[OSD([subQ1])],"isStart":false})});}
            var Q1;
            {var subQ0=sQuery(id+"F0.wireOp",EDGE,"E0.left");Q1=makeQuery(id+"F3.boolean.opBoolean","SPLIT",EDGE,{"disambiguationData":[TD([makeQuery(id+"F3.opExtrude","SWEPT_FACE",FACE,{"disambiguationData":[OSD([sQuery(id+"F2.wireOp",EDGE,"E4.top")])]})])],"derivedFrom":makeQuery(id+"F1.opExtrude","CAP_EDGE",EDGE,{"disambiguationData":[OSD([subQ0])],"isStart":false})});}
            var Q2;
            {var subQ0=sQuery(id+"F0.wireOp",EDGE,"E0.left");Q2=makeQuery(id+"F3.boolean.opBoolean","SPLIT",EDGE,{"disambiguationData":[TD([makeQuery(id+"F3.opExtrude","SWEPT_FACE",FACE,{"disambiguationData":[OSD([sQuery(id+"F2.wireOp",EDGE,"E7.1.0.3")])]})])],"derivedFrom":makeQuery(id+"F1.opExtrude","CAP_EDGE",EDGE,{"disambiguationData":[OSD([subQ0])],"isStart":false})});}
            var Q3;
            {var subQ0=sQuery(id+"F0.wireOp",EDGE,"E0.left");Q3=makeQuery(id+"F3.boolean.opBoolean","SPLIT",EDGE,{"disambiguationData":[TD([makeQuery(id+"F3.opExtrude","SWEPT_FACE",FACE,{"disambiguationData":[OSD([sQuery(id+"F2.wireOp",EDGE,"E7.2.0.3")])]})])],"derivedFrom":makeQuery(id+"F1.opExtrude","CAP_EDGE",EDGE,{"disambiguationData":[OSD([subQ0])],"isStart":false})});}
            var Q4;
            {var subQ0=sQuery(id+"F0.wireOp",EDGE,"E0.left");Q4=makeQuery(id+"F3.boolean.opBoolean","SPLIT",EDGE,{"disambiguationData":[TD([makeQuery(id+"F3.opExtrude","SWEPT_FACE",FACE,{"disambiguationData":[OSD([sQuery(id+"F2.wireOp",EDGE,"E7.3.0.3")])]})])],"derivedFrom":makeQuery(id+"F1.opExtrude","CAP_EDGE",EDGE,{"disambiguationData":[OSD([subQ0])],"isStart":false})});}
            var Q5;
            {var subQ0=sQuery(id+"F0.wireOp",EDGE,"E0.left");Q5=makeQuery(id+"F3.boolean.opBoolean","SPLIT",EDGE,{"disambiguationData":[TD([makeQuery(id+"F3.opExtrude","SWEPT_FACE",FACE,{"disambiguationData":[OSD([sQuery(id+"F2.wireOp",EDGE,"E7.4.0.3")])]})])],"derivedFrom":makeQuery(id+"F1.opExtrude","CAP_EDGE",EDGE,{"disambiguationData":[OSD([subQ0])],"isStart":false})});}
            var Q6;
            {var subQ0=sQuery(id+"F0.wireOp",EDGE,"E0.left");Q6=makeQuery(id+"F3.boolean.opBoolean","SPLIT",EDGE,{"disambiguationData":[TD([makeQuery(id+"F3.opExtrude","SWEPT_FACE",FACE,{"disambiguationData":[OSD([sQuery(id+"F2.wireOp",EDGE,"E7.5.0.3")])]})])],"derivedFrom":makeQuery(id+"F1.opExtrude","CAP_EDGE",EDGE,{"disambiguationData":[OSD([subQ0])],"isStart":false})});}
            var Q7;
            {var subQ0=sQuery(id+"F0.wireOp",EDGE,"E0.left");Q7=makeQuery(id+"F3.boolean.opBoolean","SPLIT",EDGE,{"disambiguationData":[TD([makeQuery(id+"F3.opExtrude","SWEPT_FACE",FACE,{"disambiguationData":[OSD([sQuery(id+"F2.wireOp",EDGE,"E7.6.0.3")])]})])],"derivedFrom":makeQuery(id+"F1.opExtrude","CAP_EDGE",EDGE,{"disambiguationData":[OSD([subQ0])],"isStart":false})});}
            var Q8;
            {var subQ0=sQuery(id+"F0.wireOp",EDGE,"E0.left");Q8=makeQuery(id+"F3.boolean.opBoolean","SPLIT",EDGE,{"disambiguationData":[TD([makeQuery(id+"F3.opExtrude","SWEPT_FACE",FACE,{"disambiguationData":[OSD([sQuery(id+"F2.wireOp",EDGE,"E7.7.0.3")])]})])],"derivedFrom":makeQuery(id+"F1.opExtrude","CAP_EDGE",EDGE,{"disambiguationData":[OSD([subQ0])],"isStart":false})});}
            var Q9;
            {var subQ0=sQuery(id+"F0.wireOp",EDGE,"E0.left");Q9=makeQuery(id+"F3.boolean.opBoolean","SPLIT",EDGE,{"disambiguationData":[TD([makeQuery(id+"F3.opExtrude","SWEPT_FACE",FACE,{"disambiguationData":[OSD([sQuery(id+"F2.wireOp",EDGE,"E7.8.0.3")])]})])],"derivedFrom":makeQuery(id+"F1.opExtrude","CAP_EDGE",EDGE,{"disambiguationData":[OSD([subQ0])],"isStart":false})});}
            var Q10;
            {var subQ0=sQuery(id+"F0.wireOp",EDGE,"E0.left");Q10=makeQuery(id+"F3.boolean.opBoolean","SPLIT",EDGE,{"disambiguationData":[TD([makeQuery(id+"F3.opExtrude","SWEPT_FACE",FACE,{"disambiguationData":[OSD([sQuery(id+"F2.wireOp",EDGE,"E7.9.0.3")])]})])],"derivedFrom":makeQuery(id+"F1.opExtrude","CAP_EDGE",EDGE,{"disambiguationData":[OSD([subQ0])],"isStart":false})});}
            var Q11;
            {var subQ0=sQuery(id+"F0.wireOp",EDGE,"E0.left");Q11=makeQuery(id+"F3.boolean.opBoolean","SPLIT",EDGE,{"disambiguationData":[TD([makeQuery(id+"F3.opExtrude","SWEPT_FACE",FACE,{"disambiguationData":[OSD([sQuery(id+"F2.wireOp",EDGE,"E7.10.0.3")])]})])],"derivedFrom":makeQuery(id+"F1.opExtrude","CAP_EDGE",EDGE,{"disambiguationData":[OSD([subQ0])],"isStart":false})});}
            var Q12;
            {var subQ0=sQuery(id+"F0.wireOp",EDGE,"E0.left");var subQ1=sQuery(id+"F0.wireOp",EDGE,"E0.top");Q12=makeQuery(id+"F3.boolean.opBoolean","SPLIT",EDGE,{"disambiguationData":[TD([makeQuery(id+"F1.opExtrude","SWEPT_FACE",FACE,{"disambiguationData":[OSD([subQ1])]})])],"derivedFrom":makeQuery(id+"F1.opExtrude","CAP_EDGE",EDGE,{"disambiguationData":[OSD([subQ0])],"isStart":false})});}
            var Q13;
            Q13=makeQuery(id+"F9.boolean.opBoolean","INTERSECT",EDGE,{"derivedFrom":[makeQuery(id+"F1.opExtrude","SWEPT_FACE",FACE,{"disambiguationData":[OSD([sQuery(id+"F0.wireOp",EDGE,"E0.left")])]}),makeQuery(id+"F9.opExtrude","SWEPT_FACE",FACE,{"disambiguationData":[OSD([sQuery(id+"F8.wireOp",EDGE,"E82")])]})]});
            var Q14;
            {var subQ0=sQuery(id+"F0.wireOp",EDGE,"E0.bottom");var subQ1=sQuery(id+"F0.wireOp",EDGE,"E0.right");Q14=makeQuery(id+"F3.boolean.opBoolean","SPLIT",EDGE,{"disambiguationData":[TD([makeQuery(id+"F1.opExtrude","SWEPT_FACE",FACE,{"disambiguationData":[OSD([subQ0])]})])],"derivedFrom":makeQuery(id+"F1.opExtrude","CAP_EDGE",EDGE,{"disambiguationData":[OSD([subQ1])],"isStart":false})});}
            var Q15;
            {var subQ0=sQuery(id+"F0.wireOp",EDGE,"E0.right");Q15=makeQuery(id+"F3.boolean.opBoolean","SPLIT",EDGE,{"disambiguationData":[TD([makeQuery(id+"F3.opExtrude","SWEPT_FACE",FACE,{"disambiguationData":[OSD([sQuery(id+"F2.wireOp",EDGE,"E57.MirrorCS")])]})])],"derivedFrom":makeQuery(id+"F1.opExtrude","CAP_EDGE",EDGE,{"disambiguationData":[OSD([subQ0])],"isStart":false})});}
            var Q16;
            {var subQ0=sQuery(id+"F0.wireOp",EDGE,"E0.right");Q16=makeQuery(id+"F3.boolean.opBoolean","SPLIT",EDGE,{"disambiguationData":[TD([makeQuery(id+"F3.opExtrude","SWEPT_FACE",FACE,{"disambiguationData":[OSD([sQuery(id+"F2.wireOp",EDGE,"E61.MirrorCS")])]})])],"derivedFrom":makeQuery(id+"F1.opExtrude","CAP_EDGE",EDGE,{"disambiguationData":[OSD([subQ0])],"isStart":false})});}
            var Q17;
            {var subQ0=sQuery(id+"F0.wireOp",EDGE,"E0.right");Q17=makeQuery(id+"F3.boolean.opBoolean","SPLIT",EDGE,{"disambiguationData":[TD([makeQuery(id+"F3.opExtrude","SWEPT_FACE",FACE,{"disambiguationData":[OSD([sQuery(id+"F2.wireOp",EDGE,"E72.MirrorCS")])]})])],"derivedFrom":makeQuery(id+"F1.opExtrude","CAP_EDGE",EDGE,{"disambiguationData":[OSD([subQ0])],"isStart":false})});}
            var Q18;
            {var subQ0=sQuery(id+"F0.wireOp",EDGE,"E0.right");Q18=makeQuery(id+"F3.boolean.opBoolean","SPLIT",EDGE,{"disambiguationData":[TD([makeQuery(id+"F3.opExtrude","SWEPT_FACE",FACE,{"disambiguationData":[OSD([sQuery(id+"F2.wireOp",EDGE,"E64.MirrorCS")])]})])],"derivedFrom":makeQuery(id+"F1.opExtrude","CAP_EDGE",EDGE,{"disambiguationData":[OSD([subQ0])],"isStart":false})});}
            var Q19;
            {var subQ0=sQuery(id+"F0.wireOp",EDGE,"E0.right");Q19=makeQuery(id+"F3.boolean.opBoolean","SPLIT",EDGE,{"disambiguationData":[TD([makeQuery(id+"F3.opExtrude","SWEPT_FACE",FACE,{"disambiguationData":[OSD([sQuery(id+"F2.wireOp",EDGE,"E70.MirrorCS")])]})])],"derivedFrom":makeQuery(id+"F1.opExtrude","CAP_EDGE",EDGE,{"disambiguationData":[OSD([subQ0])],"isStart":false})});}
            var Q20;
            {var subQ0=sQuery(id+"F0.wireOp",EDGE,"E0.right");Q20=makeQuery(id+"F3.boolean.opBoolean","SPLIT",EDGE,{"disambiguationData":[TD([makeQuery(id+"F3.opExtrude","SWEPT_FACE",FACE,{"disambiguationData":[OSD([sQuery(id+"F2.wireOp",EDGE,"E63.MirrorCS")])]})])],"derivedFrom":makeQuery(id+"F1.opExtrude","CAP_EDGE",EDGE,{"disambiguationData":[OSD([subQ0])],"isStart":false})});}
            var Q21;
            {var subQ0=sQuery(id+"F0.wireOp",EDGE,"E0.right");Q21=makeQuery(id+"F3.boolean.opBoolean","SPLIT",EDGE,{"disambiguationData":[TD([makeQuery(id+"F3.opExtrude","SWEPT_FACE",FACE,{"disambiguationData":[OSD([sQuery(id+"F2.wireOp",EDGE,"E71.MirrorCS")])]})])],"derivedFrom":makeQuery(id+"F1.opExtrude","CAP_EDGE",EDGE,{"disambiguationData":[OSD([subQ0])],"isStart":false})});}
            var Q22;
            {var subQ0=sQuery(id+"F0.wireOp",EDGE,"E0.right");Q22=makeQuery(id+"F3.boolean.opBoolean","SPLIT",EDGE,{"disambiguationData":[TD([makeQuery(id+"F3.opExtrude","SWEPT_FACE",FACE,{"disambiguationData":[OSD([sQuery(id+"F2.wireOp",EDGE,"E65.MirrorCS")])]})])],"derivedFrom":makeQuery(id+"F1.opExtrude","CAP_EDGE",EDGE,{"disambiguationData":[OSD([subQ0])],"isStart":false})});}
            var Q23;
            {var subQ0=sQuery(id+"F0.wireOp",EDGE,"E0.right");Q23=makeQuery(id+"F3.boolean.opBoolean","SPLIT",EDGE,{"disambiguationData":[TD([makeQuery(id+"F3.opExtrude","SWEPT_FACE",FACE,{"disambiguationData":[OSD([sQuery(id+"F2.wireOp",EDGE,"E58.MirrorCS")])]})])],"derivedFrom":makeQuery(id+"F1.opExtrude","CAP_EDGE",EDGE,{"disambiguationData":[OSD([subQ0])],"isStart":false})});}
            var Q24;
            {var subQ0=sQuery(id+"F0.wireOp",EDGE,"E0.right");Q24=makeQuery(id+"F3.boolean.opBoolean","SPLIT",EDGE,{"disambiguationData":[TD([makeQuery(id+"F3.opExtrude","SWEPT_FACE",FACE,{"disambiguationData":[OSD([sQuery(id+"F2.wireOp",EDGE,"E56.MirrorCS")])]})])],"derivedFrom":makeQuery(id+"F1.opExtrude","CAP_EDGE",EDGE,{"disambiguationData":[OSD([subQ0])],"isStart":false})});}
            var Q25;
            {var subQ0=sQuery(id+"F0.wireOp",EDGE,"E0.right");Q25=makeQuery(id+"F3.boolean.opBoolean","SPLIT",EDGE,{"disambiguationData":[TD([makeQuery(id+"F3.opExtrude","SWEPT_FACE",FACE,{"disambiguationData":[OSD([sQuery(id+"F2.wireOp",EDGE,"E60.MirrorCS")])]})])],"derivedFrom":makeQuery(id+"F1.opExtrude","CAP_EDGE",EDGE,{"disambiguationData":[OSD([subQ0])],"isStart":false})});}
            var Q26;
            {var subQ0=sQuery(id+"F0.wireOp",EDGE,"E0.right");var subQ1=sQuery(id+"F0.wireOp",EDGE,"E0.top");Q26=makeQuery(id+"F3.boolean.opBoolean","SPLIT",EDGE,{"disambiguationData":[TD([makeQuery(id+"F1.opExtrude","SWEPT_FACE",FACE,{"disambiguationData":[OSD([subQ1])]})])],"derivedFrom":makeQuery(id+"F1.opExtrude","CAP_EDGE",EDGE,{"disambiguationData":[OSD([subQ0])],"isStart":false})});}
            var Q27;
            Q27=makeQuery(id+"F9.boolean.opBoolean","COPY",EDGE,{"derivedFrom":makeQuery(id+"F9.opExtrude","CAP_EDGE",EDGE,{"disambiguationData":[OSD([sQuery(id+"F8.wireOp",EDGE,"E82")])],"isStart":true})});
            fillet(context, id + "F12", {"entities" : qUnion([Q0, Q1, Q2, Q3, Q4, Q5, Q6, Q7, Q8, Q9, Q10, Q11, Q12, Q13, Q14, Q15, Q16, Q17, Q18, Q19, Q20, Q21, Q22, Q23, Q24, Q25, Q26, Q27]), "radius" : 2 * mm, "tangentPropagation" : true, "allowEdgeOverflow" : false});
        }
    });
